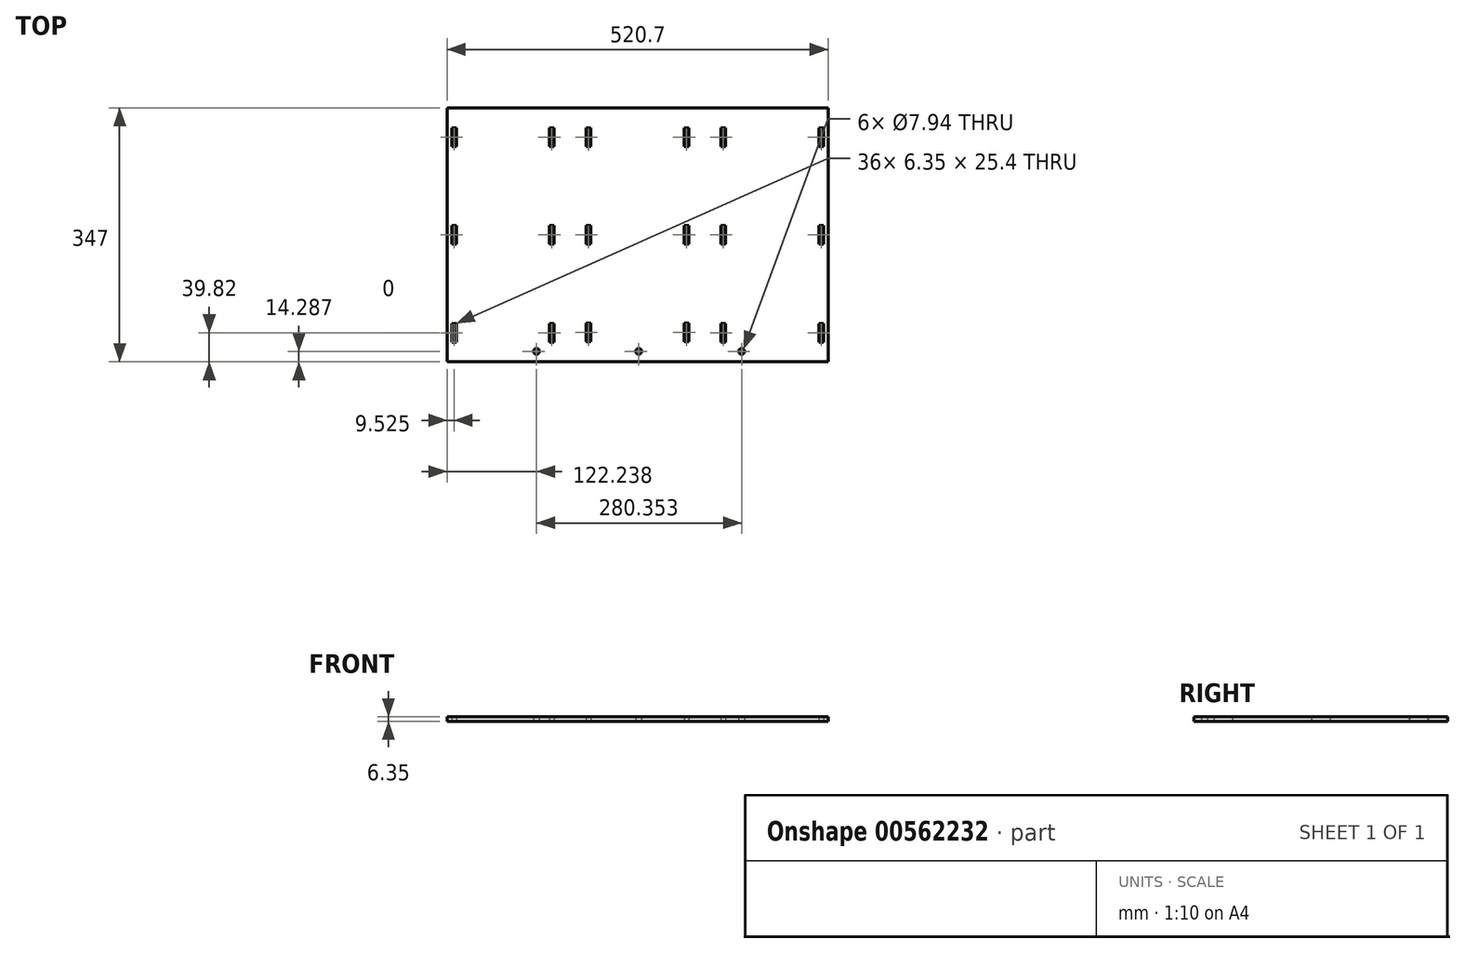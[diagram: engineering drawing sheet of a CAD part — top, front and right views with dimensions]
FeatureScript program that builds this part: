
annotation { "Feature Type Name" : "Feature", "Feature Type Description" : "" }
export const myFeature = defineFeature(function(context is Context, id is Id, definition is map)
    precondition{}
    {
        {
            var Q0;
            Q0=qCreatedBy(makeId("Top.planeOp"),FACE);
            var sketch = newSketch(context, id + "F0", { "sketchPlane" : qUnion([Q0])});
            skLineSegment(sketch, "E0.bottom", {"start": v(254, 173.5) * mm, "end": v(-254, 173.5) * mm});
            skLineSegment(sketch, "E0.top", {"start": v(254, -173.5) * mm, "end": v(-254, -173.5) * mm});
            skLineSegment(sketch, "E0.left", {"start": v(254, 173.5) * mm, "end": v(254, 146.38) * mm});
            skLineSegment(sketch, "E0.right", {"start": v(-254, 173.5) * mm, "end": v(-254, 146.38) * mm});
            skPoint(sketch, "E0.middle", {"position": v(0, 0) * mm});
            skCircle(sketch, "E1", {"center": v(-138.11, -159.21) * mm, "radius": 3.97 * mm});
            skCircle(sketch, "E2", {"center": v(1.59, -159.21) * mm, "radius": 3.97 * mm});
            skCircle(sketch, "E3", {"center": v(142.24, -159.21) * mm, "radius": 3.97 * mm});
            skLineSegment(sketch, "E4", {"start": v(-254, 12.7) * mm, "end": v(-247.65, 12.7) * mm});
            skLineSegment(sketch, "E5", {"start": v(-247.65, 12.7) * mm, "end": v(-247.65, -12.7) * mm});
            skLineSegment(sketch, "E6", {"start": v(-247.65, -12.7) * mm, "end": v(-254, -12.7) * mm});
            skLineSegment(sketch, "E7", {"start": v(254, 12.7) * mm, "end": v(247.65, 12.7) * mm});
            skLineSegment(sketch, "E8", {"start": v(247.65, 12.7) * mm, "end": v(247.65, -12.7) * mm});
            skLineSegment(sketch, "E9", {"start": v(247.65, -12.7) * mm, "end": v(254, -12.7) * mm});
            skLineSegment(sketch, "E10.bottom", {"start": v(-120.35, 12.7) * mm, "end": v(-114, 12.7) * mm});
            skLineSegment(sketch, "E10.top", {"start": v(-120.35, -12.7) * mm, "end": v(-114, -12.7) * mm});
            skLineSegment(sketch, "E10.left", {"start": v(-120.35, 12.7) * mm, "end": v(-120.35, -12.7) * mm});
            skLineSegment(sketch, "E10.right", {"start": v(-114, 12.7) * mm, "end": v(-114, -12.7) * mm});
            skLineSegment(sketch, "E11.bottom", {"start": v(-70, 12.7) * mm, "end": v(-63.65, 12.7) * mm});
            skLineSegment(sketch, "E11.top", {"start": v(-70, -12.7) * mm, "end": v(-63.65, -12.7) * mm});
            skLineSegment(sketch, "E11.left", {"start": v(-70, 12.7) * mm, "end": v(-70, -12.7) * mm});
            skLineSegment(sketch, "E11.right", {"start": v(-63.65, 12.7) * mm, "end": v(-63.65, -12.7) * mm});
            skLineSegment(sketch, "E12.bottom", {"start": v(63.65, 12.7) * mm, "end": v(70, 12.7) * mm});
            skLineSegment(sketch, "E12.top", {"start": v(63.65, -12.7) * mm, "end": v(70, -12.7) * mm});
            skLineSegment(sketch, "E12.left", {"start": v(63.65, 12.7) * mm, "end": v(63.65, -12.7) * mm});
            skLineSegment(sketch, "E12.right", {"start": v(70, 12.7) * mm, "end": v(70, -12.7) * mm});
            skLineSegment(sketch, "E13.bottom", {"start": v(114, 12.7) * mm, "end": v(120.35, 12.7) * mm});
            skLineSegment(sketch, "E13.top", {"start": v(114, -12.7) * mm, "end": v(120.35, -12.7) * mm});
            skLineSegment(sketch, "E13.left", {"start": v(114, 12.7) * mm, "end": v(114, -12.7) * mm});
            skLineSegment(sketch, "E13.right", {"start": v(120.35, 12.7) * mm, "end": v(120.35, -12.7) * mm});
            skLineSegment(sketch, "E14", {"start": v(-254, 146.38) * mm, "end": v(-247.65, 146.38) * mm});
            skLineSegment(sketch, "E15", {"start": v(-247.65, 146.38) * mm, "end": v(-247.65, 120.98) * mm});
            skLineSegment(sketch, "E16", {"start": v(-247.65, 120.98) * mm, "end": v(-254, 120.98) * mm});
            skLineSegment(sketch, "E17", {"start": v(-254, -120.98) * mm, "end": v(-247.65, -120.98) * mm});
            skLineSegment(sketch, "E18", {"start": v(-247.65, -120.98) * mm, "end": v(-247.65, -146.38) * mm});
            skLineSegment(sketch, "E19", {"start": v(-247.65, -146.38) * mm, "end": v(-254, -146.38) * mm});
            skLineSegment(sketch, "E20", {"start": v(254, 146.38) * mm, "end": v(247.65, 146.38) * mm});
            skLineSegment(sketch, "E21", {"start": v(247.65, 146.38) * mm, "end": v(247.65, 120.98) * mm});
            skLineSegment(sketch, "E22", {"start": v(247.65, 120.98) * mm, "end": v(254, 120.98) * mm});
            skLineSegment(sketch, "E23", {"start": v(254, -146.38) * mm, "end": v(247.65, -146.38) * mm});
            skLineSegment(sketch, "E24", {"start": v(247.65, -146.38) * mm, "end": v(247.65, -120.98) * mm});
            skLineSegment(sketch, "E25", {"start": v(247.65, -120.98) * mm, "end": v(254, -120.98) * mm});
            skLineSegment(sketch, "E26.bottom", {"start": v(114, -120.98) * mm, "end": v(120.35, -120.98) * mm});
            skLineSegment(sketch, "E26.top", {"start": v(114, -146.38) * mm, "end": v(120.35, -146.38) * mm});
            skLineSegment(sketch, "E26.left", {"start": v(114, -120.98) * mm, "end": v(114, -146.38) * mm});
            skLineSegment(sketch, "E26.right", {"start": v(120.35, -120.98) * mm, "end": v(120.35, -146.38) * mm});
            skPoint(sketch, "E27.oppositeSnap0", {"position": v(120.35, -133.68) * mm});
            skLineSegment(sketch, "E27.bottom", {"start": v(114, 146.38) * mm, "end": v(120.35, 146.38) * mm});
            skLineSegment(sketch, "E27.top", {"start": v(114, 120.98) * mm, "end": v(120.35, 120.98) * mm});
            skLineSegment(sketch, "E27.left", {"start": v(114, 146.38) * mm, "end": v(114, 120.98) * mm});
            skLineSegment(sketch, "E27.right", {"start": v(120.35, 146.38) * mm, "end": v(120.35, 120.98) * mm});
            skLineSegment(sketch, "E28.bottom", {"start": v(63.65, 146) * mm, "end": v(70, 146) * mm});
            skLineSegment(sketch, "E28.top", {"start": v(63.65, 120.6) * mm, "end": v(70, 120.6) * mm});
            skLineSegment(sketch, "E28.left", {"start": v(63.65, 146) * mm, "end": v(63.65, 120.6) * mm});
            skLineSegment(sketch, "E28.right", {"start": v(70, 146) * mm, "end": v(70, 120.6) * mm});
            skLineSegment(sketch, "E29.bottom", {"start": v(63.65, -120.6) * mm, "end": v(70, -120.6) * mm});
            skLineSegment(sketch, "E29.top", {"start": v(63.65, -146) * mm, "end": v(70, -146) * mm});
            skLineSegment(sketch, "E29.left", {"start": v(63.65, -120.6) * mm, "end": v(63.65, -146) * mm});
            skLineSegment(sketch, "E29.right", {"start": v(70, -120.6) * mm, "end": v(70, -146) * mm});
            skLineSegment(sketch, "E30.bottom", {"start": v(-70, -120.6) * mm, "end": v(-63.65, -120.6) * mm});
            skLineSegment(sketch, "E30.top", {"start": v(-70, -146) * mm, "end": v(-63.65, -146) * mm});
            skLineSegment(sketch, "E30.left", {"start": v(-70, -120.6) * mm, "end": v(-70, -146) * mm});
            skLineSegment(sketch, "E30.right", {"start": v(-63.65, -120.6) * mm, "end": v(-63.65, -146) * mm});
            skLineSegment(sketch, "E31.bottom", {"start": v(-120.35, -120.98) * mm, "end": v(-114, -120.98) * mm});
            skLineSegment(sketch, "E31.top", {"start": v(-120.35, -146.38) * mm, "end": v(-114, -146.38) * mm});
            skLineSegment(sketch, "E31.left", {"start": v(-120.35, -120.98) * mm, "end": v(-120.35, -146.38) * mm});
            skLineSegment(sketch, "E31.right", {"start": v(-114, -120.98) * mm, "end": v(-114, -146.38) * mm});
            skLineSegment(sketch, "E32.bottom", {"start": v(-120.35, 146.38) * mm, "end": v(-114, 146.38) * mm});
            skLineSegment(sketch, "E32.top", {"start": v(-120.35, 120.98) * mm, "end": v(-114, 120.98) * mm});
            skLineSegment(sketch, "E32.left", {"start": v(-120.35, 146.38) * mm, "end": v(-120.35, 120.98) * mm});
            skLineSegment(sketch, "E32.right", {"start": v(-114, 146.38) * mm, "end": v(-114, 120.98) * mm});
            skLineSegment(sketch, "E33.bottom", {"start": v(-70, 146) * mm, "end": v(-63.65, 146) * mm});
            skLineSegment(sketch, "E33.top", {"start": v(-70, 120.6) * mm, "end": v(-63.65, 120.6) * mm});
            skLineSegment(sketch, "E33.left", {"start": v(-70, 146) * mm, "end": v(-70, 120.6) * mm});
            skLineSegment(sketch, "E33.right", {"start": v(-63.65, 146) * mm, "end": v(-63.65, 120.6) * mm});
            skLineSegment(sketch, "E34.trimOffspring", {"start": v(-254, 120.98) * mm, "end": v(-254, 12.7) * mm});
            skLineSegment(sketch, "E35.trimOffspring", {"start": v(-254, -146.38) * mm, "end": v(-254, -173.5) * mm});
            skLineSegment(sketch, "E36.trimOffspring", {"start": v(254, -146.38) * mm, "end": v(254, -173.5) * mm});
            skLineSegment(sketch, "E37.trimOffspring", {"start": v(254, -12.7) * mm, "end": v(254, -120.98) * mm});
            skLineSegment(sketch, "E38.trimOffspring", {"start": v(254, 120.98) * mm, "end": v(254, 12.7) * mm});
            skLineSegment(sketch, "E39", {"start": v(-254, 173.5) * mm, "end": v(-260.35, 173.5) * mm});
            skLineSegment(sketch, "E40", {"start": v(-260.35, 173.5) * mm, "end": v(-260.35, -173.5) * mm});
            skLineSegment(sketch, "E41", {"start": v(-260.35, -173.5) * mm, "end": v(-254, -173.5) * mm});
            skLineSegment(sketch, "E42", {"start": v(254, 173.5) * mm, "end": v(260.35, 173.5) * mm});
            skLineSegment(sketch, "E43", {"start": v(260.35, 173.5) * mm, "end": v(260.35, -173.5) * mm});
            skLineSegment(sketch, "E44", {"start": v(260.35, -173.5) * mm, "end": v(254, -173.5) * mm});
            skLineSegment(sketch, "E45", {"start": v(-254, -120.98) * mm, "end": v(-254, -146.38) * mm});
            skLineSegment(sketch, "E46", {"start": v(-254, 12.7) * mm, "end": v(-254, -12.7) * mm});
            skLineSegment(sketch, "E47", {"start": v(-254, 146.38) * mm, "end": v(-254, 120.98) * mm});
            skLineSegment(sketch, "E48", {"start": v(254, 146.38) * mm, "end": v(254, 120.98) * mm});
            skLineSegment(sketch, "E49", {"start": v(254, 12.7) * mm, "end": v(254, -12.7) * mm});
            skLineSegment(sketch, "E50", {"start": v(254, -120.98) * mm, "end": v(254, -146.38) * mm});
            skSolve(sketch);
        }
        {
            var Q0;
            Q0 = qSketchRegion(id + "F0", true);
            extrude(context, id + "F1", {"entities" : qUnion([Q0]), "depth" : 6.35 * mm, "offsetDistance" : 25.4 * mm});
        }
    });
